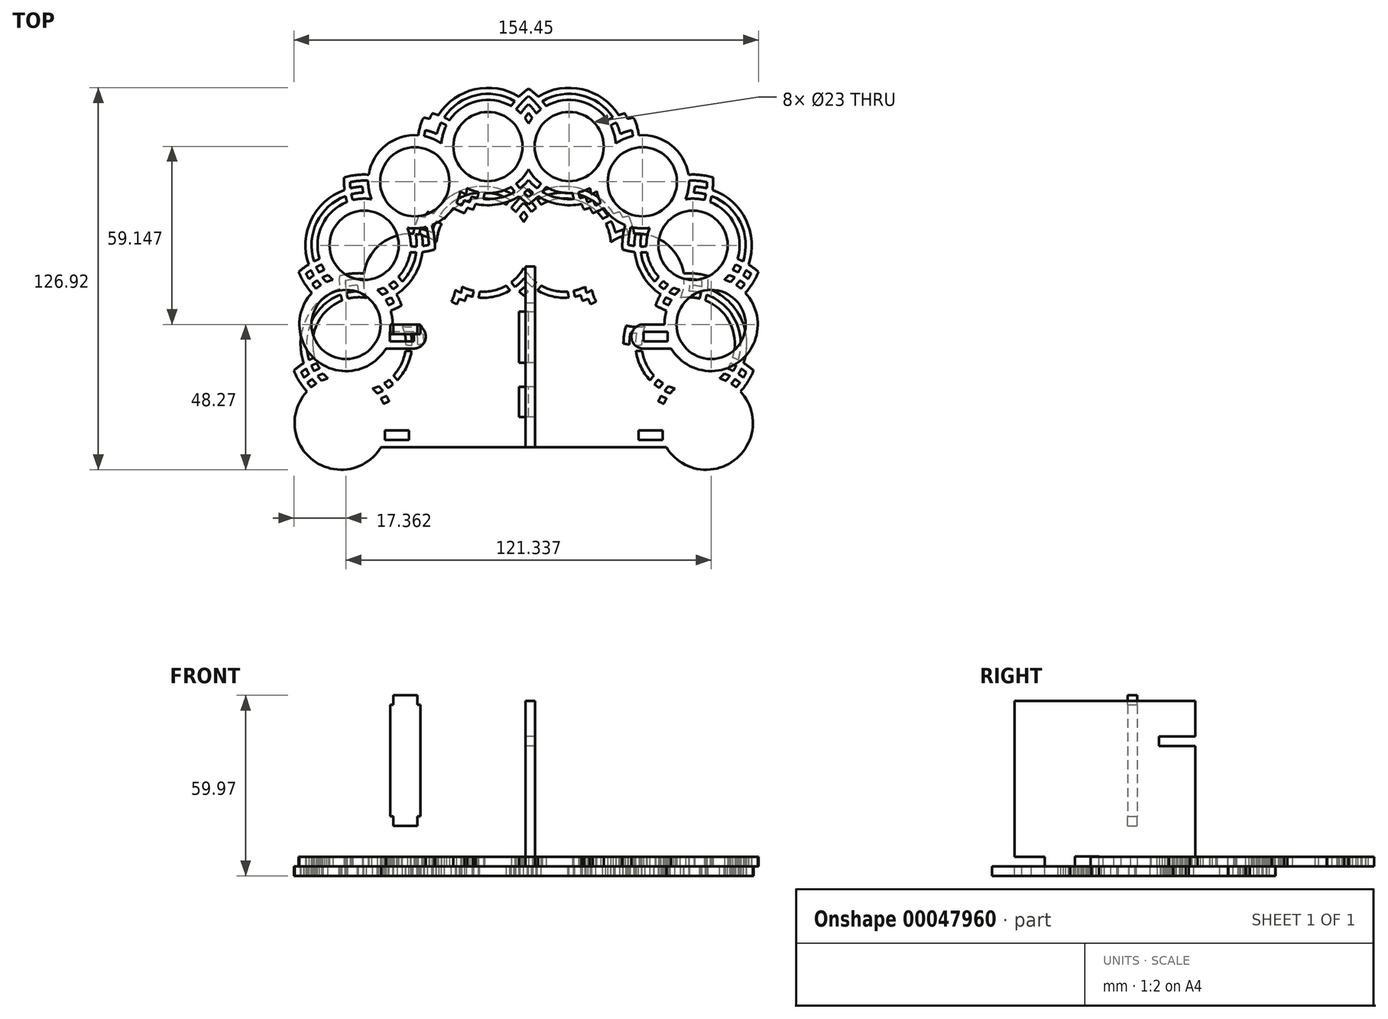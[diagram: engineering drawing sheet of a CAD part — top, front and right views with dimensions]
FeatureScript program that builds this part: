
annotation { "Feature Type Name" : "Feature", "Feature Type Description" : "" }
export const myFeature = defineFeature(function(context is Context, id is Id, definition is map)
    precondition{}
    {
        {
            var Q0;
            Q0=qCreatedBy(makeId("Top.planeOp"),FACE);
            var sketch = newSketch(context, id + "F0", { "sketchPlane" : qUnion([Q0])});
            skCircle(sketch, "E0", {"center": v(-59.67, 0) * mm, "radius": 11.5 * mm});
            skArc(sketch, "E1.0", {"start": v(-64.09, 14.86) * mm, "mid": v(-65.14, 14.5) * mm, "end": v(-66.16, 14.08) * mm});
            skArc(sketch, "E2.0", {"start": v(-66.82, 18.14) * mm, "mid": v(-67.75, 17.75) * mm, "end": v(-68.66, 17.3) * mm});
            skArc(sketch, "E3.0", {"start": v(-67.77, 19.91) * mm, "mid": v(-68.7, 19.52) * mm, "end": v(-69.59, 19.07) * mm});
            skArc(sketch, "E4.0", {"start": v(-65.62, 16.46) * mm, "mid": v(-66.58, 16.08) * mm, "end": v(-67.52, 15.64) * mm});
            skArc(sketch, "E5.0", {"start": v(-68.48, 21.78) * mm, "mid": v(-69.4, 21.39) * mm, "end": v(-70.32, 20.95) * mm});
            skArc(sketch, "E6.1.0", {"start": v(-52.15, 49.77) * mm, "mid": v(-56.25, 49.68) * mm, "end": v(-60.28, 48.87) * mm});
            skArc(sketch, "E6.1.1", {"start": v(-53.95, 43.82) * mm, "mid": v(-55.95, 43.67) * mm, "end": v(-57.92, 43.3) * mm});
            skArc(sketch, "E6.1.2", {"start": v(-52.32, 47.78) * mm, "mid": v(-55.34, 47.76) * mm, "end": v(-58.33, 47.31) * mm});
            skArc(sketch, "E6.1.3", {"start": v(-54.25, 45.81) * mm, "mid": v(-56.25, 45.65) * mm, "end": v(-58.22, 45.28) * mm});
            skArc(sketch, "E6.1.4", {"start": v(-51.2, 41.63) * mm, "mid": v(-54.34, 41.8) * mm, "end": v(-57.45, 41.35) * mm});
            skCircle(sketch, "E6.1.5", {"center": v(-53.66, 26.32) * mm, "radius": 11.5 * mm});
            skArc(sketch, "E6.2.0", {"start": v(-25.29, 67.9) * mm, "mid": v(-26.18, 68.38) * mm, "end": v(-27.08, 68.82) * mm});
            skArc(sketch, "E6.2.1", {"start": v(-29.5, 63.32) * mm, "mid": v(-31.36, 64.06) * mm, "end": v(-33.3, 64.57) * mm});
            skArc(sketch, "E6.2.2", {"start": v(-26.31, 66.19) * mm, "mid": v(-27.2, 66.65) * mm, "end": v(-28.1, 67.08) * mm});
            skArc(sketch, "E6.2.4", {"start": v(-27.97, 60.15) * mm, "mid": v(-30.72, 61.68) * mm, "end": v(-33.72, 62.62) * mm});
            skCircle(sketch, "E6.2.5", {"center": v(-36.83, 47.43) * mm, "radius": 11.5 * mm});
            skArc(sketch, "E6.3.0", {"start": v(6.78, 72.59) * mm, "mid": v(6.18, 73.4) * mm, "end": v(5.56, 74.19) * mm});
            skArc(sketch, "E6.3.1", {"start": v(2.22, 68.6) * mm, "mid": v(1.64, 69.46) * mm, "end": v(1, 70.28) * mm});
            skArc(sketch, "E6.3.2", {"start": v(5.11, 71.48) * mm, "mid": v(3.21, 73.83) * mm, "end": v(1, 75.88) * mm});
            skArc(sketch, "E6.3.3", {"start": v(3.6, 70.16) * mm, "mid": v(2.38, 71.76) * mm, "end": v(1, 73.22) * mm});
            skArc(sketch, "E6.3.4", {"start": v(1, 66.76) * mm, "mid": v(0.42, 67.7) * mm, "end": v(-0.22, 68.6) * mm});
            skCircle(sketch, "E6.3.5", {"center": v(-12.5, 59.15) * mm, "radius": 11.5 * mm});
            skArc(sketch, "E6.4.0", {"start": v(-4.78, 45.7) * mm, "mid": v(-4.18, 44.9) * mm, "end": v(-3.56, 44.1) * mm});
            skArc(sketch, "E6.4.1", {"start": v(1, 48.01) * mm, "mid": v(2.36, 46.54) * mm, "end": v(3.89, 45.23) * mm});
            skArc(sketch, "E6.4.2", {"start": v(-3.11, 46.81) * mm, "mid": v(-2.52, 46) * mm, "end": v(-1.89, 45.23) * mm});
            skArc(sketch, "E6.4.3", {"start": v(1, 45.08) * mm, "mid": v(1.74, 44.4) * mm, "end": v(2.52, 43.76) * mm});
            skArc(sketch, "E6.4.4", {"start": v(1, 51.53) * mm, "mid": v(2.82, 48.96) * mm, "end": v(5.11, 46.81) * mm});
            skCircle(sketch, "E6.4.5", {"center": v(14.5, 59.15) * mm, "radius": 11.5 * mm});
            skArc(sketch, "E6.5.0", {"start": v(15.63, 43.69) * mm, "mid": v(15.8, 42.7) * mm, "end": v(16.03, 41.71) * mm});
            skArc(sketch, "E6.5.1", {"start": v(21.46, 45.3) * mm, "mid": v(21.61, 44.27) * mm, "end": v(21.83, 43.26) * mm});
            skArc(sketch, "E6.5.2", {"start": v(17.6, 43.96) * mm, "mid": v(17.8, 42.98) * mm, "end": v(18.02, 42) * mm});
            skArc(sketch, "E6.5.3", {"start": v(19.96, 42.52) * mm, "mid": v(20.23, 41.56) * mm, "end": v(20.56, 40.61) * mm});
            skArc(sketch, "E6.5.4", {"start": v(23.66, 44.24) * mm, "mid": v(24.21, 42.27) * mm, "end": v(25.02, 40.4) * mm});
            skCircle(sketch, "E6.5.5", {"center": v(38.83, 47.43) * mm, "radius": 11.5 * mm});
            skArc(sketch, "E6.6.0", {"start": v(74.34, 12.07) * mm, "mid": v(76.06, 14.65) * mm, "end": v(77.42, 17.44) * mm});
            skArc(sketch, "E6.6.1", {"start": v(68.16, 14.08) * mm, "mid": v(68.86, 14.84) * mm, "end": v(69.52, 15.64) * mm});
            skArc(sketch, "E6.6.2", {"start": v(71.6, 11.9) * mm, "mid": v(72.26, 12.65) * mm, "end": v(72.87, 13.44) * mm});
            skArc(sketch, "E6.6.3", {"start": v(69.98, 13.08) * mm, "mid": v(70.64, 13.84) * mm, "end": v(71.27, 14.63) * mm});
            skArc(sketch, "E6.6.4", {"start": v(41.29, 32.13) * mm, "mid": v(40.41, 29.1) * mm, "end": v(40.16, 25.97) * mm});
            skCircle(sketch, "E6.6.5", {"center": v(55.66, 26.32) * mm, "radius": 11.5 * mm});
            skArc(sketch, "E6.7.0", {"start": v(44.28, 15.8) * mm, "mid": v(43.61, 15.04) * mm, "end": v(42.99, 14.26) * mm});
            skArc(sketch, "E6.7.2", {"start": v(45.73, 14.43) * mm, "mid": v(45.07, 13.67) * mm, "end": v(44.45, 12.88) * mm});
            skArc(sketch, "E6.7.3", {"start": v(47.35, 13.24) * mm, "mid": v(46.69, 12.48) * mm, "end": v(46.06, 11.7) * mm});
            skArc(sketch, "E6.7.4", {"start": v(51.24, 11.47) * mm, "mid": v(50.45, 10.7) * mm, "end": v(49.71, 9.86) * mm});
            skCircle(sketch, "E6.7.5", {"center": v(61.67, 0) * mm, "radius": 11.5 * mm});
            skPoint(sketch, "E6.center", {"position": v(1, 0) * mm});
            skLineSegment(sketch, "E6.anchor1", {"start": v(1, 0) * mm, "end": v(-59.67, 0) * mm, "construction": true});
            skLineSegment(sketch, "E6.anchor2", {"start": v(1, 0) * mm, "end": v(61.67, 0) * mm, "construction": true});
            skArc(sketch, "E7.trimOffspring", {"start": v(-21.66, 44.24) * mm, "mid": v(-20.76, 43.72) * mm, "end": v(-19.83, 43.26) * mm});
            skArc(sketch, "E8.trimOffspring", {"start": v(-20.42, 41.33) * mm, "mid": v(-19.5, 40.95) * mm, "end": v(-18.56, 40.61) * mm});
            skArc(sketch, "E9.trimOffspring", {"start": v(-23.02, 40.4) * mm, "mid": v(-22.13, 39.93) * mm, "end": v(-21.23, 39.5) * mm});
            skArc(sketch, "E10.trimOffspring", {"start": v(-24.04, 38.67) * mm, "mid": v(-22.23, 37.76) * mm, "end": v(-20.35, 37) * mm});
            skArc(sketch, "E11.trimOffspring", {"start": v(-38.34, 23.98) * mm, "mid": v(-37.33, 23.94) * mm, "end": v(-36.32, 23.94) * mm});
            skArc(sketch, "E12.trimOffspring", {"start": v(-38.16, 25.97) * mm, "mid": v(-37.16, 25.94) * mm, "end": v(-36.16, 25.94) * mm});
            skArc(sketch, "E13.trimOffspring", {"start": v(-36.54, 29.93) * mm, "mid": v(-35.53, 29.98) * mm, "end": v(-34.53, 30.08) * mm});
            skArc(sketch, "E14.trimOffspring", {"start": v(-44.85, 4.54) * mm, "mid": v(-43, 5.38) * mm, "end": v(-41.24, 6.37) * mm});
            skArc(sketch, "E15.trimOffspring", {"start": v(-45.56, 6.4) * mm, "mid": v(-44.64, 6.8) * mm, "end": v(-43.74, 7.25) * mm});
            skArc(sketch, "E16.trimOffspring", {"start": v(-46.5, 8.18) * mm, "mid": v(-45.58, 8.58) * mm, "end": v(-44.67, 9.02) * mm});
            skArc(sketch, "E17.trimOffspring", {"start": v(-47.71, 9.86) * mm, "mid": v(-46.75, 10.25) * mm, "end": v(-45.8, 10.68) * mm});
            skArc(sketch, "E18.trimOffspring", {"start": v(61.35, 40.74) * mm, "mid": v(61.62, 41.71) * mm, "end": v(61.84, 42.7) * mm});
            skArc(sketch, "E19.trimOffspring", {"start": v(59.45, 41.35) * mm, "mid": v(59.7, 42.32) * mm, "end": v(59.92, 43.3) * mm});
            skArc(sketch, "E20.trimOffspring", {"start": v(55.95, 43.82) * mm, "mid": v(56.13, 44.81) * mm, "end": v(56.25, 45.81) * mm});
            skArc(sketch, "E21.trimOffspring", {"start": v(38.54, 29.93) * mm, "mid": v(38.24, 27.95) * mm, "end": v(38.16, 25.94) * mm});
            skArc(sketch, "E22.trimOffspring", {"start": v(36.53, 30.08) * mm, "mid": v(36.24, 28.1) * mm, "end": v(36.16, 26.1) * mm});
            skArc(sketch, "E23.trimOffspring", {"start": v(33.13, 33.02) * mm, "mid": v(32.31, 29) * mm, "end": v(32.2, 24.88) * mm});
            skArc(sketch, "E24.trimOffspring", {"start": v(37.7, 62.9) * mm, "mid": v(37.02, 65.87) * mm, "end": v(35.95, 68.74) * mm});
            skArc(sketch, "E25.trimOffspring", {"start": v(35.72, 62.62) * mm, "mid": v(35.53, 63.6) * mm, "end": v(35.3, 64.57) * mm});
            skArc(sketch, "E26.trimOffspring", {"start": v(31.5, 63.32) * mm, "mid": v(30.9, 65.24) * mm, "end": v(30.1, 67.08) * mm});
            skArc(sketch, "E27.trimOffspring", {"start": v(29.97, 60.15) * mm, "mid": v(29.45, 63.25) * mm, "end": v(28.31, 66.19) * mm});
            skArc(sketch, "E28.trimOffspring", {"start": v(35.04, 32.4) * mm, "mid": v(34.39, 29.45) * mm, "end": v(34.16, 26.44) * mm});
            skArc(sketch, "E29.trimOffspring", {"start": v(53.2, 41.63) * mm, "mid": v(54.07, 44.65) * mm, "end": v(54.32, 47.78) * mm});
            skArc(sketch, "E30.trimOffspring", {"start": v(-19.46, 45.3) * mm, "mid": v(-17.58, 44.5) * mm, "end": v(-15.6, 43.96) * mm});
            skArc(sketch, "E31.trimOffspring", {"start": v(66.09, 14.86) * mm, "mid": v(66.88, 15.63) * mm, "end": v(67.62, 16.46) * mm});
            skArc(sketch, "E32.trimOffspring", {"start": v(-49.24, 11.47) * mm, "mid": v(-48.2, 11.82) * mm, "end": v(-47.17, 12.25) * mm});
            skArc(sketch, "E33.trimOffspring", {"start": v(-39.29, 32.13) * mm, "mid": v(-36.15, 31.95) * mm, "end": v(-33.04, 32.4) * mm});
            skArc(sketch, "E34.trimOffspring", {"start": v(-41.24, 6.37) * mm, "mid": v(-42, 8.25) * mm, "end": v(-42.95, 10.03) * mm});
            skArc(sketch, "E35.trimOffspring", {"start": v(-43.74, 7.25) * mm, "mid": v(-44.18, 8.15) * mm, "end": v(-44.67, 9.02) * mm});
            skArc(sketch, "E36.trimOffspring", {"start": v(77.42, 17.44) * mm, "mid": v(75.8, 18.77) * mm, "end": v(74.09, 19.95) * mm});
            skArc(sketch, "E37.trimOffspring", {"start": v(74.98, 16.89) * mm, "mid": v(74.17, 17.5) * mm, "end": v(73.33, 18.07) * mm});
            skArc(sketch, "E38.trimOffspring", {"start": v(74, 15.1) * mm, "mid": v(73.2, 15.72) * mm, "end": v(72.38, 16.3) * mm});
            skArc(sketch, "E39.trimOffspring", {"start": v(71.6, 11.9) * mm, "mid": v(70.8, 12.52) * mm, "end": v(69.98, 13.08) * mm});
            skArc(sketch, "E40.trimOffspring", {"start": v(-75.42, 17.44) * mm, "mid": v(-73.54, 13.79) * mm, "end": v(-71.05, 10.52) * mm});
            skArc(sketch, "E41.trimOffspring", {"start": v(-72.98, 16.89) * mm, "mid": v(-72.51, 15.98) * mm, "end": v(-72, 15.1) * mm});
            skArc(sketch, "E42.trimOffspring", {"start": v(-30.95, 70.19) * mm, "mid": v(-31.46, 69.29) * mm, "end": v(-31.92, 68.37) * mm});
            skArc(sketch, "E43.trimOffspring", {"start": v(-33.95, 68.74) * mm, "mid": v(-35.02, 65.87) * mm, "end": v(-35.7, 62.9) * mm});
            skArc(sketch, "E44.trimOffspring", {"start": v(1, 78.38) * mm, "mid": v(-0.65, 77.11) * mm, "end": v(-2.19, 75.7) * mm});
            skArc(sketch, "E45.trimOffspring", {"start": v(1, 75.88) * mm, "mid": v(-1.21, 73.83) * mm, "end": v(-3.11, 71.48) * mm});
            skArc(sketch, "E46.trimOffspring", {"start": v(62.28, 48.87) * mm, "mid": v(58.25, 49.68) * mm, "end": v(54.15, 49.77) * mm});
            skArc(sketch, "E47.trimOffspring", {"start": v(60.33, 47.31) * mm, "mid": v(57.34, 47.76) * mm, "end": v(54.32, 47.78) * mm});
            skArc(sketch, "E48.trimOffspring", {"start": v(22.35, 37) * mm, "mid": v(24.23, 37.76) * mm, "end": v(26.04, 38.67) * mm});
            skArc(sketch, "E49.trimOffspring", {"start": v(19.4, 38.21) * mm, "mid": v(20.39, 38.47) * mm, "end": v(21.36, 38.77) * mm});
            skArc(sketch, "E50.trimOffspring", {"start": v(1, 39.91) * mm, "mid": v(2.65, 41.18) * mm, "end": v(4.19, 42.6) * mm});
            skArc(sketch, "E51.trimOffspring", {"start": v(1, 42.41) * mm, "mid": v(1.78, 43.07) * mm, "end": v(2.52, 43.76) * mm});
            skArc(sketch, "E52.trimOffspring", {"start": v(43.24, 6.37) * mm, "mid": v(44.12, 5.85) * mm, "end": v(45.01, 5.37) * mm});
            skArc(sketch, "E53.trimOffspring", {"start": v(-30.2, 24.88) * mm, "mid": v(-30.31, 29) * mm, "end": v(-31.13, 33.02) * mm});
            skArc(sketch, "E54.trimOffspring", {"start": v(-32.16, 26.44) * mm, "mid": v(-32.39, 29.45) * mm, "end": v(-33.04, 32.4) * mm});
            skArc(sketch, "E55.trimOffspring", {"start": v(-54.25, 45.81) * mm, "mid": v(-54.13, 44.81) * mm, "end": v(-53.95, 43.82) * mm});
            skArc(sketch, "E56.trimOffspring", {"start": v(-58.33, 47.31) * mm, "mid": v(-58.3, 46.3) * mm, "end": v(-58.22, 45.28) * mm});
            skArc(sketch, "E57.trimOffspring", {"start": v(-60.28, 48.87) * mm, "mid": v(-60.32, 46.79) * mm, "end": v(-60.17, 44.7) * mm});
            skArc(sketch, "E58.trimOffspring", {"start": v(35.3, 64.57) * mm, "mid": v(33.36, 64.06) * mm, "end": v(31.5, 63.32) * mm});
            skArc(sketch, "E59.trimOffspring", {"start": v(35.95, 68.74) * mm, "mid": v(34.93, 68.58) * mm, "end": v(33.92, 68.37) * mm});
            skArc(sketch, "E60.trimOffspring", {"start": v(32.95, 70.19) * mm, "mid": v(31.96, 69.9) * mm, "end": v(30.97, 69.58) * mm});
            skArc(sketch, "E61.trimOffspring", {"start": v(-28.97, 69.58) * mm, "mid": v(-29.96, 69.9) * mm, "end": v(-30.95, 70.19) * mm});
            skArc(sketch, "E62.trimOffspring", {"start": v(-28.1, 67.08) * mm, "mid": v(-28.9, 65.24) * mm, "end": v(-29.5, 63.32) * mm});
            skArc(sketch, "E63.trimOffspring", {"start": v(-26.31, 66.19) * mm, "mid": v(-27.45, 63.25) * mm, "end": v(-27.97, 60.15) * mm});
            skArc(sketch, "E64.trimOffspring", {"start": v(-4.78, 72.59) * mm, "mid": v(-15.95, 74.26) * mm, "end": v(-25.29, 67.9) * mm});
            skArc(sketch, "E65.trimOffspring", {"start": v(-3.56, 74.19) * mm, "mid": v(-16.4, 76.2) * mm, "end": v(-27.08, 68.82) * mm});
            skArc(sketch, "E66.trimOffspring", {"start": v(-3.56, 74.19) * mm, "mid": v(-4.18, 73.4) * mm, "end": v(-4.78, 72.59) * mm});
            skArc(sketch, "E67.trimOffspring", {"start": v(4.19, 75.7) * mm, "mid": v(2.65, 77.11) * mm, "end": v(1, 78.38) * mm});
            skArc(sketch, "E68.trimOffspring", {"start": v(5.11, 71.48) * mm, "mid": v(4.33, 70.84) * mm, "end": v(3.6, 70.16) * mm});
            skArc(sketch, "E69.trimOffspring", {"start": v(29.08, 68.82) * mm, "mid": v(28.18, 68.38) * mm, "end": v(27.29, 67.9) * mm});
            skArc(sketch, "E70.trimOffspring", {"start": v(29.08, 68.82) * mm, "mid": v(18.4, 76.2) * mm, "end": v(5.56, 74.19) * mm});
            skArc(sketch, "E71.trimOffspring", {"start": v(27.29, 67.9) * mm, "mid": v(17.95, 74.26) * mm, "end": v(6.78, 72.59) * mm});
            skArc(sketch, "E72.trimOffspring", {"start": v(62.17, 44.7) * mm, "mid": v(62.32, 46.79) * mm, "end": v(62.28, 48.87) * mm});
            skArc(sketch, "E73.trimOffspring", {"start": v(59.92, 43.3) * mm, "mid": v(57.95, 43.67) * mm, "end": v(55.95, 43.82) * mm});
            skArc(sketch, "E74.trimOffspring", {"start": v(59.45, 41.35) * mm, "mid": v(56.34, 41.8) * mm, "end": v(53.2, 41.63) * mm});
            skArc(sketch, "E75.trimOffspring", {"start": v(72.32, 20.95) * mm, "mid": v(71.4, 21.39) * mm, "end": v(70.48, 21.78) * mm});
            skArc(sketch, "E76.trimOffspring", {"start": v(72.32, 20.95) * mm, "mid": v(71.43, 33.92) * mm, "end": v(61.84, 42.7) * mm});
            skArc(sketch, "E77.trimOffspring", {"start": v(70.48, 21.78) * mm, "mid": v(69.63, 33.05) * mm, "end": v(61.35, 40.74) * mm});
            skArc(sketch, "E78.trimOffspring", {"start": v(-59.84, 42.7) * mm, "mid": v(-59.62, 41.71) * mm, "end": v(-59.35, 40.74) * mm});
            skArc(sketch, "E79.trimOffspring", {"start": v(-59.84, 42.7) * mm, "mid": v(-69.43, 33.92) * mm, "end": v(-70.32, 20.95) * mm});
            skArc(sketch, "E80.trimOffspring", {"start": v(-59.35, 40.74) * mm, "mid": v(-67.63, 33.05) * mm, "end": v(-68.48, 21.78) * mm});
            skArc(sketch, "E81.trimOffspring", {"start": v(-72.09, 19.95) * mm, "mid": v(-73.8, 18.77) * mm, "end": v(-75.42, 17.44) * mm});
            skArc(sketch, "E82.trimOffspring", {"start": v(-69.59, 19.07) * mm, "mid": v(-69.15, 18.18) * mm, "end": v(-68.66, 17.3) * mm});
            skArc(sketch, "E83.trimOffspring", {"start": v(-67.77, 19.91) * mm, "mid": v(-67.33, 19.01) * mm, "end": v(-66.82, 18.14) * mm});
            skArc(sketch, "E84.trimOffspring", {"start": v(-36.16, 25.94) * mm, "mid": v(-36.24, 27.95) * mm, "end": v(-36.54, 29.93) * mm});
            skArc(sketch, "E85.trimOffspring", {"start": v(-34.3, 24.07) * mm, "mid": v(-32.23, 24.39) * mm, "end": v(-30.2, 24.88) * mm});
            skArc(sketch, "E86.trimOffspring", {"start": v(-38.16, 25.97) * mm, "mid": v(-38.41, 29.1) * mm, "end": v(-39.29, 32.13) * mm});
            skArc(sketch, "E87.trimOffspring", {"start": v(-42.28, 15.8) * mm, "mid": v(-39.7, 19.6) * mm, "end": v(-38.34, 23.98) * mm});
            skArc(sketch, "E88.trimOffspring", {"start": v(-40.99, 14.26) * mm, "mid": v(-37.9, 18.73) * mm, "end": v(-36.32, 23.94) * mm});
            skArc(sketch, "E89.trimOffspring", {"start": v(-40.99, 14.26) * mm, "mid": v(-41.61, 15.04) * mm, "end": v(-42.28, 15.8) * mm});
            skArc(sketch, "E90.trimOffspring", {"start": v(-21.23, 39.5) * mm, "mid": v(-20.8, 40.4) * mm, "end": v(-20.42, 41.33) * mm});
            skArc(sketch, "E91.trimOffspring", {"start": v(-20.35, 37) * mm, "mid": v(-19.83, 37.87) * mm, "end": v(-19.36, 38.77) * mm});
            skArc(sketch, "E92.trimOffspring", {"start": v(-17.4, 38.21) * mm, "mid": v(-16.99, 39.14) * mm, "end": v(-16.62, 40.09) * mm});
            skArc(sketch, "E93.trimOffspring", {"start": v(32.2, 24.88) * mm, "mid": v(34.23, 24.39) * mm, "end": v(36.3, 24.07) * mm});
            skArc(sketch, "E94.trimOffspring", {"start": v(34.16, 26.44) * mm, "mid": v(35.16, 26.25) * mm, "end": v(36.16, 26.1) * mm});
            skArc(sketch, "E95.trimOffspring", {"start": v(36.53, 30.08) * mm, "mid": v(37.53, 29.98) * mm, "end": v(38.54, 29.93) * mm});
            skArc(sketch, "E96.trimOffspring", {"start": v(18.02, 42) * mm, "mid": v(19, 42.23) * mm, "end": v(19.96, 42.52) * mm});
            skArc(sketch, "E97.trimOffspring", {"start": v(17.6, 43.96) * mm, "mid": v(19.58, 44.5) * mm, "end": v(21.46, 45.3) * mm});
            skArc(sketch, "E98.trimOffspring", {"start": v(5.56, 44.1) * mm, "mid": v(6.18, 44.9) * mm, "end": v(6.78, 45.7) * mm});
            skArc(sketch, "E99.trimOffspring", {"start": v(5.56, 44.1) * mm, "mid": v(10.6, 42.09) * mm, "end": v(16.03, 41.71) * mm});
            skArc(sketch, "E100.trimOffspring", {"start": v(6.78, 45.7) * mm, "mid": v(11.05, 44.04) * mm, "end": v(15.63, 43.69) * mm});
            skArc(sketch, "E101.trimOffspring", {"start": v(-14.03, 41.71) * mm, "mid": v(-13.8, 42.7) * mm, "end": v(-13.63, 43.69) * mm});
            skArc(sketch, "E102.trimOffspring", {"start": v(-14.03, 41.71) * mm, "mid": v(-8.6, 42.09) * mm, "end": v(-3.56, 44.1) * mm});
            skArc(sketch, "E103.trimOffspring", {"start": v(-13.63, 43.69) * mm, "mid": v(-9.05, 44.04) * mm, "end": v(-4.78, 45.7) * mm});
            skArc(sketch, "E104.trimOffspring", {"start": v(-3.11, 46.81) * mm, "mid": v(-0.82, 48.96) * mm, "end": v(1, 51.53) * mm});
            skArc(sketch, "E105.trimOffspring", {"start": v(-1.89, 45.23) * mm, "mid": v(-0.36, 46.54) * mm, "end": v(1, 48.01) * mm});
            skArc(sketch, "E106.trimOffspring", {"start": v(-2.19, 42.6) * mm, "mid": v(-0.65, 41.18) * mm, "end": v(1, 39.91) * mm});
            skArc(sketch, "E107.trimOffspring", {"start": v(38.32, 23.94) * mm, "mid": v(39.33, 23.94) * mm, "end": v(40.34, 23.98) * mm});
            skArc(sketch, "E108.trimOffspring", {"start": v(38.32, 23.94) * mm, "mid": v(39.9, 18.73) * mm, "end": v(42.99, 14.26) * mm});
            skArc(sketch, "E109.trimOffspring", {"start": v(40.34, 23.98) * mm, "mid": v(41.7, 19.6) * mm, "end": v(44.28, 15.8) * mm});
            skArc(sketch, "E110.trimOffspring", {"start": v(45.73, 14.43) * mm, "mid": v(46.52, 13.8) * mm, "end": v(47.35, 13.24) * mm});
            skArc(sketch, "E111.trimOffspring", {"start": v(44.45, 12.88) * mm, "mid": v(45.24, 12.26) * mm, "end": v(46.06, 11.7) * mm});
            skArc(sketch, "E112.trimOffspring", {"start": v(-2.19, 75.7) * mm, "mid": v(-16.84, 78.16) * mm, "end": v(-28.97, 69.58) * mm});
            skArc(sketch, "E113.trimOffspring", {"start": v(1, 73.22) * mm, "mid": v(-0.38, 71.76) * mm, "end": v(-1.6, 70.16) * mm});
            skArc(sketch, "E114.trimOffspring", {"start": v(-0.52, 43.76) * mm, "mid": v(0.26, 44.4) * mm, "end": v(1, 45.08) * mm});
            skArc(sketch, "E115.trimOffspring", {"start": v(4.19, 42.6) * mm, "mid": v(11.16, 39.94) * mm, "end": v(18.62, 40.09) * mm});
            skArc(sketch, "E116.trimOffspring", {"start": v(-0.52, 43.76) * mm, "mid": v(0.22, 43.07) * mm, "end": v(1, 42.41) * mm});
            skArc(sketch, "E117.trimOffspring", {"start": v(3.89, 45.23) * mm, "mid": v(4.52, 46) * mm, "end": v(5.11, 46.81) * mm});
            skArc(sketch, "E118.trimOffspring", {"start": v(-1.6, 70.16) * mm, "mid": v(-2.33, 70.84) * mm, "end": v(-3.11, 71.48) * mm});
            skArc(sketch, "E119.trimOffspring", {"start": v(1, 70.28) * mm, "mid": v(0.36, 69.46) * mm, "end": v(-0.22, 68.6) * mm});
            skArc(sketch, "E120.trimOffspring", {"start": v(2.22, 68.6) * mm, "mid": v(1.58, 67.7) * mm, "end": v(1, 66.76) * mm});
            skArc(sketch, "E121.trimOffspring", {"start": v(-35.7, 62.9) * mm, "mid": v(-46.5, 59.55) * mm, "end": v(-52.15, 49.77) * mm});
            skArc(sketch, "E122.trimOffspring", {"start": v(-33.3, 64.57) * mm, "mid": v(-33.53, 63.6) * mm, "end": v(-33.72, 62.62) * mm});
            skArc(sketch, "E123.trimOffspring", {"start": v(-31.92, 68.37) * mm, "mid": v(-32.93, 68.58) * mm, "end": v(-33.95, 68.74) * mm});
            skArc(sketch, "E124.trimOffspring", {"start": v(30.97, 69.58) * mm, "mid": v(18.84, 78.16) * mm, "end": v(4.19, 75.7) * mm});
            skArc(sketch, "E125.trimOffspring", {"start": v(30.1, 67.08) * mm, "mid": v(29.2, 66.65) * mm, "end": v(28.31, 66.19) * mm});
            skArc(sketch, "E126.trimOffspring", {"start": v(33.92, 68.37) * mm, "mid": v(33.46, 69.29) * mm, "end": v(32.95, 70.19) * mm});
            skArc(sketch, "E127.trimOffspring", {"start": v(35.72, 62.62) * mm, "mid": v(32.72, 61.68) * mm, "end": v(29.97, 60.15) * mm});
            skArc(sketch, "E128.trimOffspring", {"start": v(22.42, 41.33) * mm, "mid": v(22.8, 40.4) * mm, "end": v(23.23, 39.5) * mm});
            skArc(sketch, "E129.trimOffspring", {"start": v(21.83, 43.26) * mm, "mid": v(22.76, 43.72) * mm, "end": v(23.66, 44.24) * mm});
            skArc(sketch, "E130.trimOffspring", {"start": v(26.04, 38.67) * mm, "mid": v(29.16, 35.31) * mm, "end": v(33.13, 33.02) * mm});
            skArc(sketch, "E131.trimOffspring", {"start": v(23.23, 39.5) * mm, "mid": v(24.13, 39.93) * mm, "end": v(25.02, 40.4) * mm});
            skArc(sketch, "E132.trimOffspring", {"start": v(21.36, 38.77) * mm, "mid": v(21.83, 37.87) * mm, "end": v(22.35, 37) * mm});
            skArc(sketch, "E133.trimOffspring", {"start": v(20.56, 40.61) * mm, "mid": v(21.5, 40.95) * mm, "end": v(22.42, 41.33) * mm});
            skArc(sketch, "E134.trimOffspring", {"start": v(18.62, 40.09) * mm, "mid": v(18.99, 39.14) * mm, "end": v(19.4, 38.21) * mm});
            skArc(sketch, "E135.trimOffspring", {"start": v(-17.96, 42.52) * mm, "mid": v(-17, 42.23) * mm, "end": v(-16.02, 42) * mm});
            skArc(sketch, "E136.trimOffspring", {"start": v(-19.83, 43.26) * mm, "mid": v(-19.61, 44.27) * mm, "end": v(-19.46, 45.3) * mm});
            skArc(sketch, "E137.trimOffspring", {"start": v(-23.02, 40.4) * mm, "mid": v(-22.21, 42.27) * mm, "end": v(-21.66, 44.24) * mm});
            skArc(sketch, "E138.trimOffspring", {"start": v(-19.36, 38.77) * mm, "mid": v(-18.39, 38.47) * mm, "end": v(-17.4, 38.21) * mm});
            skArc(sketch, "E139.trimOffspring", {"start": v(-18.56, 40.61) * mm, "mid": v(-18.23, 41.56) * mm, "end": v(-17.96, 42.52) * mm});
            skArc(sketch, "E140.trimOffspring", {"start": v(-16.62, 40.09) * mm, "mid": v(-9.16, 39.94) * mm, "end": v(-2.19, 42.6) * mm});
            skArc(sketch, "E141.trimOffspring", {"start": v(-16.02, 42) * mm, "mid": v(-15.8, 42.98) * mm, "end": v(-15.6, 43.96) * mm});
            skArc(sketch, "E142.trimOffspring", {"start": v(38.16, 25.94) * mm, "mid": v(39.16, 25.94) * mm, "end": v(40.16, 25.97) * mm});
            skArc(sketch, "E143.trimOffspring", {"start": v(36.3, 24.07) * mm, "mid": v(39.06, 16.09) * mm, "end": v(44.95, 10.03) * mm});
            skArc(sketch, "E144.trimOffspring", {"start": v(35.04, 32.4) * mm, "mid": v(38.15, 31.95) * mm, "end": v(41.29, 32.13) * mm});
            skArc(sketch, "E145.trimOffspring", {"start": v(60.22, 45.28) * mm, "mid": v(60.3, 46.3) * mm, "end": v(60.33, 47.31) * mm});
            skArc(sketch, "E146.trimOffspring", {"start": v(60.22, 45.28) * mm, "mid": v(58.25, 45.65) * mm, "end": v(56.25, 45.81) * mm});
            skArc(sketch, "E147.trimOffspring", {"start": v(54.15, 49.77) * mm, "mid": v(48.5, 59.55) * mm, "end": v(37.7, 62.9) * mm});
            skArc(sketch, "E148.trimOffspring", {"start": v(-34.16, 26.1) * mm, "mid": v(-33.16, 26.25) * mm, "end": v(-32.16, 26.44) * mm});
            skArc(sketch, "E149.trimOffspring", {"start": v(-31.13, 33.02) * mm, "mid": v(-27.16, 35.31) * mm, "end": v(-24.04, 38.67) * mm});
            skArc(sketch, "E150.trimOffspring", {"start": v(-34.16, 26.1) * mm, "mid": v(-34.24, 28.1) * mm, "end": v(-34.53, 30.08) * mm});
            skArc(sketch, "E151.trimOffspring", {"start": v(-57.92, 43.3) * mm, "mid": v(-57.7, 42.32) * mm, "end": v(-57.45, 41.35) * mm});
            skArc(sketch, "E152.trimOffspring", {"start": v(-60.17, 44.7) * mm, "mid": v(-71.23, 34.78) * mm, "end": v(-72.09, 19.95) * mm});
            skArc(sketch, "E153.trimOffspring", {"start": v(-52.32, 47.78) * mm, "mid": v(-52.07, 44.65) * mm, "end": v(-51.2, 41.63) * mm});
            skArc(sketch, "E154.trimOffspring", {"start": v(-65.62, 16.46) * mm, "mid": v(-64.88, 15.63) * mm, "end": v(-64.09, 14.86) * mm});
            skArc(sketch, "E155.trimOffspring", {"start": v(-67.52, 15.64) * mm, "mid": v(-66.86, 14.84) * mm, "end": v(-66.16, 14.08) * mm});
            skArc(sketch, "E156.trimOffspring", {"start": v(-69.27, 14.63) * mm, "mid": v(-70.09, 14.06) * mm, "end": v(-70.87, 13.44) * mm});
            skArc(sketch, "E157.trimOffspring", {"start": v(-67.98, 13.08) * mm, "mid": v(-68.8, 12.52) * mm, "end": v(-69.6, 11.9) * mm});
            skArc(sketch, "E158.trimOffspring", {"start": v(-71.05, 10.52) * mm, "mid": v(-68.98, -12.4) * mm, "end": v(-46.4, -8) * mm});
            skArc(sketch, "E159.trimOffspring", {"start": v(-71.33, 18.07) * mm, "mid": v(-70.88, 17.17) * mm, "end": v(-70.38, 16.3) * mm});
            skArc(sketch, "E160.trimOffspring", {"start": v(-69.27, 14.63) * mm, "mid": v(-68.64, 13.84) * mm, "end": v(-67.98, 13.08) * mm});
            skArc(sketch, "E161.trimOffspring", {"start": v(-70.87, 13.44) * mm, "mid": v(-70.26, 12.65) * mm, "end": v(-69.6, 11.9) * mm});
            skArc(sketch, "E162.trimOffspring", {"start": v(-70.38, 16.3) * mm, "mid": v(-71.2, 15.72) * mm, "end": v(-72, 15.1) * mm});
            skArc(sketch, "E163.trimOffspring", {"start": v(-71.33, 18.07) * mm, "mid": v(-72.17, 17.5) * mm, "end": v(-72.98, 16.89) * mm});
            skArc(sketch, "E164.trimOffspring", {"start": v(71.59, 19.07) * mm, "mid": v(70.7, 19.52) * mm, "end": v(69.77, 19.91) * mm});
            skArc(sketch, "E165.trimOffspring", {"start": v(70.66, 17.3) * mm, "mid": v(69.75, 17.75) * mm, "end": v(68.82, 18.14) * mm});
            skArc(sketch, "E166.trimOffspring", {"start": v(69.52, 15.64) * mm, "mid": v(68.58, 16.08) * mm, "end": v(67.62, 16.46) * mm});
            skArc(sketch, "E167.trimOffspring", {"start": v(68.16, 14.08) * mm, "mid": v(67.14, 14.5) * mm, "end": v(66.09, 14.86) * mm});
            skArc(sketch, "E168.trimOffspring", {"start": v(70.66, 17.3) * mm, "mid": v(71.15, 18.18) * mm, "end": v(71.59, 19.07) * mm});
            skArc(sketch, "E169.trimOffspring", {"start": v(68.82, 18.14) * mm, "mid": v(69.33, 19.01) * mm, "end": v(69.77, 19.91) * mm});
            skArc(sketch, "E170.trimOffspring", {"start": v(72.38, 16.3) * mm, "mid": v(72.88, 17.17) * mm, "end": v(73.33, 18.07) * mm});
            skArc(sketch, "E171.trimOffspring", {"start": v(74, 15.1) * mm, "mid": v(74.51, 15.98) * mm, "end": v(74.98, 16.89) * mm});
            skArc(sketch, "E172.trimOffspring", {"start": v(74.09, 19.95) * mm, "mid": v(73.23, 34.78) * mm, "end": v(62.17, 44.7) * mm});
            skArc(sketch, "E173.trimOffspring", {"start": v(49.17, 12.25) * mm, "mid": v(50.2, 11.82) * mm, "end": v(51.24, 11.47) * mm});
            skArc(sketch, "E174.trimOffspring", {"start": v(47.8, 10.68) * mm, "mid": v(48.75, 10.25) * mm, "end": v(49.71, 9.86) * mm});
            skArc(sketch, "E175.trimOffspring", {"start": v(44.95, 10.03) * mm, "mid": v(44, 8.25) * mm, "end": v(43.24, 6.37) * mm});
            skArc(sketch, "E176.trimOffspring", {"start": v(46.67, 9.02) * mm, "mid": v(46.18, 8.15) * mm, "end": v(45.74, 7.25) * mm});
            skArc(sketch, "E177.trimOffspring", {"start": v(46.67, 9.02) * mm, "mid": v(47.58, 8.58) * mm, "end": v(48.5, 8.18) * mm});
            skArc(sketch, "E178.trimOffspring", {"start": v(45.74, 7.25) * mm, "mid": v(46.64, 6.8) * mm, "end": v(47.56, 6.4) * mm});
            skArc(sketch, "E179.trimOffspring", {"start": v(-45.35, 13.24) * mm, "mid": v(-44.52, 13.8) * mm, "end": v(-43.73, 14.43) * mm});
            skArc(sketch, "E180.trimOffspring", {"start": v(-44.06, 11.7) * mm, "mid": v(-43.24, 12.26) * mm, "end": v(-42.45, 12.88) * mm});
            skArc(sketch, "E181.trimOffspring", {"start": v(-45.8, 10.68) * mm, "mid": v(-46.47, 11.49) * mm, "end": v(-47.17, 12.25) * mm});
            skArc(sketch, "E182.trimOffspring", {"start": v(-47.71, 9.86) * mm, "mid": v(-48.45, 10.7) * mm, "end": v(-49.24, 11.47) * mm});
            skArc(sketch, "E183.trimOffspring", {"start": v(-42.45, 12.88) * mm, "mid": v(-43.07, 13.67) * mm, "end": v(-43.73, 14.43) * mm});
            skArc(sketch, "E184.trimOffspring", {"start": v(-44.06, 11.7) * mm, "mid": v(-44.69, 12.48) * mm, "end": v(-45.35, 13.24) * mm});
            skArc(sketch, "E185.trimOffspring", {"start": v(-42.95, 10.03) * mm, "mid": v(-37.06, 16.09) * mm, "end": v(-34.3, 24.07) * mm});
            skArc(sketch, "E186.trimOffspring", {"start": v(-45.56, 6.4) * mm, "mid": v(-46, 7.31) * mm, "end": v(-46.5, 8.18) * mm});
            skArc(sketch, "E187.0", {"start": v(72.87, 13.44) * mm, "mid": v(72.09, 14.06) * mm, "end": v(71.27, 14.63) * mm});
            skArc(sketch, "E188.0", {"start": v(43.24, 6.37) * mm, "mid": v(45, 5.38) * mm, "end": v(46.85, 4.54) * mm});
            skArc(sketch, "E189.trimOffspring", {"start": v(73.05, 10.52) * mm, "mid": v(73.71, 11.28) * mm, "end": v(74.34, 12.07) * mm});
            skArc(sketch, "E190.trimOffspring", {"start": v(49.17, 12.25) * mm, "mid": v(48.47, 11.49) * mm, "end": v(47.8, 10.68) * mm});
            skArc(sketch, "E191.trimOffspring", {"start": v(48.5, 8.18) * mm, "mid": v(48, 7.31) * mm, "end": v(47.56, 6.4) * mm});
            skArc(sketch, "E192.trimOffspring", {"start": v(46.85, 4.54) * mm, "mid": v(46.34, 2.3) * mm, "end": v(46.17, 0) * mm});
            skLineSegment(sketch, "E193", {"start": v(-44.17, 0) * mm, "end": v(-37.17, 0) * mm});
            skArc(sketch, "E194", {"start": v(-37.17, -8) * mm, "mid": v(-33.17, -4) * mm, "end": v(-37.17, 0) * mm});
            skLineSegment(sketch, "E195.rect.bottom", {"start": v(-37.17, -5.59) * mm, "end": v(-45.17, -5.59) * mm});
            skLineSegment(sketch, "E195.rect.top", {"start": v(-37.17, -2.41) * mm, "end": v(-45.17, -2.41) * mm});
            skLineSegment(sketch, "E195.rect.right", {"start": v(-45.17, -5.59) * mm, "end": v(-45.17, -2.41) * mm});
            skLineSegment(sketch, "E196", {"start": v(46.17, 0) * mm, "end": v(39.17, 0) * mm});
            skLineSegment(sketch, "E197", {"start": v(39.17, -2.41) * mm, "end": v(39.17, -4) * mm});
            skArc(sketch, "E198", {"start": v(39.17, 0) * mm, "mid": v(35.17, -4) * mm, "end": v(39.17, -8) * mm});
            skLineSegment(sketch, "E199.rect.bottom", {"start": v(47.17, -5.59) * mm, "end": v(39.17, -5.59) * mm});
            skLineSegment(sketch, "E199.rect.top", {"start": v(47.17, -2.41) * mm, "end": v(39.17, -2.41) * mm});
            skLineSegment(sketch, "E199.rect.left", {"start": v(47.17, -5.59) * mm, "end": v(47.17, -2.41) * mm});
            skLineSegment(sketch, "E199.rect.right", {"start": v(39.17, -5.59) * mm, "end": v(39.17, -4) * mm});
            skLineSegment(sketch, "E200", {"start": v(39.17, -8) * mm, "end": v(48.4, -8) * mm});
            skLineSegment(sketch, "E201", {"start": v(-37.17, -8) * mm, "end": v(-46.4, -8) * mm});
            skArc(sketch, "E202.trimOffspring", {"start": v(-44.17, 0) * mm, "mid": v(-44.34, 2.3) * mm, "end": v(-44.85, 4.54) * mm});
            skLineSegment(sketch, "E203", {"start": v(-37.17, -2.41) * mm, "end": v(-37.17, -5.59) * mm});
            skArc(sketch, "E204.trimOffspring", {"start": v(48.4, -8) * mm, "mid": v(70.98, -12.4) * mm, "end": v(73.05, 10.52) * mm});
            skLineSegment(sketch, "E205", {"start": v(-37.17, -8) * mm, "end": v(39.17, -8) * mm, "construction": true});
            skLineSegment(sketch, "E206", {"start": v(1, 39.91) * mm, "end": v(1, -8) * mm, "construction": true});
            skSolve(sketch);
        }
        {
            var Q0;
            Q0=makeQuery(id+"F0.imprint","IMPRINT",FACE,{"disambiguationData":[TD([[makeQuery(id+"F0.imprint","IMPRINT",EDGE,{"derivedFrom":sQuery(id+"F0.wireOp",EDGE,"E0")}),-1.0]])]});
            extrude(context, id + "F1", {"entities" : qUnion([Q0]), "depth" : 3.17 * mm});
        }
        {
            var Q0;
            Q0=qCreatedBy(makeId("Top.planeOp"),FACE);
            var sketch = newSketch(context, id + "F2", { "sketchPlane" : qUnion([Q0])});
            skArc(sketch, "E207.0", {"start": v(-65.7, -17.92) * mm, "mid": v(-66.75, -18.27) * mm, "end": v(-67.77, -18.7) * mm});
            skArc(sketch, "E208.0", {"start": v(-68.44, -14.63) * mm, "mid": v(-69.36, -15.03) * mm, "end": v(-70.27, -15.47) * mm});
            skArc(sketch, "E209.0", {"start": v(-69.39, -12.86) * mm, "mid": v(-70.3, -13.26) * mm, "end": v(-71.2, -13.7) * mm});
            skArc(sketch, "E210.0", {"start": v(-67.23, -16.31) * mm, "mid": v(-68.2, -16.7) * mm, "end": v(-69.13, -17.13) * mm});
            skArc(sketch, "E211.0", {"start": v(-70.1, -10.99) * mm, "mid": v(-71.02, -11.39) * mm, "end": v(-71.93, -11.82) * mm});
            skArc(sketch, "E212.1.0", {"start": v(-53.76, 17) * mm, "mid": v(-57.87, 16.9) * mm, "end": v(-61.9, 16.1) * mm});
            skArc(sketch, "E212.1.1", {"start": v(-55.56, 11.05) * mm, "mid": v(-57.57, 10.9) * mm, "end": v(-59.54, 10.52) * mm});
            skArc(sketch, "E212.1.2", {"start": v(-53.94, 15) * mm, "mid": v(-56.95, 14.98) * mm, "end": v(-59.94, 14.54) * mm});
            skArc(sketch, "E212.1.3", {"start": v(-55.86, 13.04) * mm, "mid": v(-57.86, 12.88) * mm, "end": v(-59.83, 12.51) * mm});
            skArc(sketch, "E212.1.4", {"start": v(-52.81, 8.85) * mm, "mid": v(-55.95, 9.04) * mm, "end": v(-59.06, 8.58) * mm});
            skArc(sketch, "E212.2.0", {"start": v(-26.9, 35.13) * mm, "mid": v(-27.8, 35.6) * mm, "end": v(-28.7, 36.05) * mm});
            skArc(sketch, "E212.2.1", {"start": v(-31.1, 30.55) * mm, "mid": v(-32.98, 31.29) * mm, "end": v(-34.92, 31.8) * mm});
            skArc(sketch, "E212.2.2", {"start": v(-27.92, 33.41) * mm, "mid": v(-28.8, 33.88) * mm, "end": v(-29.71, 34.3) * mm});
            skArc(sketch, "E212.2.4", {"start": v(-29.58, 27.38) * mm, "mid": v(-32.33, 28.9) * mm, "end": v(-35.33, 29.85) * mm});
            skArc(sketch, "E212.3.0", {"start": v(5.16, 39.81) * mm, "mid": v(4.57, 40.63) * mm, "end": v(3.94, 41.42) * mm});
            skArc(sketch, "E212.3.1", {"start": v(0.6, 35.84) * mm, "mid": v(0.02, 36.7) * mm, "end": v(-0.61, 37.51) * mm});
            skArc(sketch, "E212.3.2", {"start": v(3.5, 38.7) * mm, "mid": v(1.6, 41.05) * mm, "end": v(-0.61, 43.1) * mm});
            skArc(sketch, "E212.3.3", {"start": v(1.98, 37.39) * mm, "mid": v(0.76, 38.98) * mm, "end": v(-0.61, 40.45) * mm});
            skArc(sketch, "E212.3.4", {"start": v(-0.61, 34) * mm, "mid": v(-1.2, 34.93) * mm, "end": v(-1.84, 35.84) * mm});
            skArc(sketch, "E212.4.0", {"start": v(-6.4, 12.94) * mm, "mid": v(-5.8, 12.12) * mm, "end": v(-5.17, 11.33) * mm});
            skArc(sketch, "E212.4.1", {"start": v(-0.61, 15.24) * mm, "mid": v(0.75, 13.77) * mm, "end": v(2.28, 12.46) * mm});
            skArc(sketch, "E212.4.2", {"start": v(-4.72, 14.04) * mm, "mid": v(-4.13, 13.24) * mm, "end": v(-3.5, 12.46) * mm});
            skArc(sketch, "E212.4.3", {"start": v(-0.61, 12.3) * mm, "mid": v(0.13, 11.63) * mm, "end": v(0.9, 10.99) * mm});
            skArc(sketch, "E212.4.4", {"start": v(-0.61, 18.76) * mm, "mid": v(1.2, 16.2) * mm, "end": v(3.5, 14.04) * mm});
            skArc(sketch, "E212.5.0", {"start": v(14.01, 10.92) * mm, "mid": v(14.2, 9.92) * mm, "end": v(14.42, 8.94) * mm});
            skArc(sketch, "E212.5.1", {"start": v(19.84, 12.52) * mm, "mid": v(20, 11.5) * mm, "end": v(20.22, 10.48) * mm});
            skArc(sketch, "E212.5.2", {"start": v(16, 11.19) * mm, "mid": v(16.18, 10.2) * mm, "end": v(16.4, 9.23) * mm});
            skArc(sketch, "E212.5.3", {"start": v(18.34, 9.75) * mm, "mid": v(18.62, 8.79) * mm, "end": v(18.94, 7.84) * mm});
            skArc(sketch, "E212.5.4", {"start": v(22.05, 11.46) * mm, "mid": v(22.6, 9.5) * mm, "end": v(23.4, 7.62) * mm});
            skArc(sketch, "E212.6.0", {"start": v(72.73, -20.7) * mm, "mid": v(74.44, -18.12) * mm, "end": v(75.8, -15.33) * mm});
            skArc(sketch, "E212.6.1", {"start": v(66.55, -18.7) * mm, "mid": v(67.25, -17.94) * mm, "end": v(67.9, -17.13) * mm});
            skArc(sketch, "E212.6.2", {"start": v(69.99, -20.87) * mm, "mid": v(70.64, -20.12) * mm, "end": v(71.26, -19.33) * mm});
            skArc(sketch, "E212.6.3", {"start": v(68.36, -19.69) * mm, "mid": v(69.03, -18.93) * mm, "end": v(69.65, -18.14) * mm});
            skArc(sketch, "E212.6.4", {"start": v(39.68, -0.64) * mm, "mid": v(38.8, -3.66) * mm, "end": v(38.55, -6.8) * mm});
            skArc(sketch, "E212.7.0", {"start": v(42.66, -16.97) * mm, "mid": v(42, -17.73) * mm, "end": v(41.37, -18.52) * mm});
            skArc(sketch, "E212.7.2", {"start": v(44.11, -18.35) * mm, "mid": v(43.46, -19.1) * mm, "end": v(42.84, -19.9) * mm});
            skArc(sketch, "E212.7.3", {"start": v(45.74, -19.53) * mm, "mid": v(45.07, -20.3) * mm, "end": v(44.45, -21.08) * mm});
            skArc(sketch, "E212.7.4", {"start": v(49.63, -21.3) * mm, "mid": v(48.83, -22.08) * mm, "end": v(48.1, -22.9) * mm});
            skArc(sketch, "E213.trimOffspring", {"start": v(-23.27, 11.46) * mm, "mid": v(-22.37, 10.95) * mm, "end": v(-21.44, 10.48) * mm});
            skArc(sketch, "E214.trimOffspring", {"start": v(-22.04, 8.56) * mm, "mid": v(-21.11, 8.17) * mm, "end": v(-20.17, 7.84) * mm});
            skArc(sketch, "E215.trimOffspring", {"start": v(-24.63, 7.62) * mm, "mid": v(-23.75, 7.15) * mm, "end": v(-22.84, 6.73) * mm});
            skArc(sketch, "E216.trimOffspring", {"start": v(-39.95, -8.8) * mm, "mid": v(-38.94, -8.83) * mm, "end": v(-37.94, -8.83) * mm});
            skArc(sketch, "E217.trimOffspring", {"start": v(-39.78, -6.8) * mm, "mid": v(-38.78, -6.84) * mm, "end": v(-37.78, -6.83) * mm});
            skArc(sketch, "E218.trimOffspring", {"start": v(-38.15, -2.84) * mm, "mid": v(-37.14, -2.8) * mm, "end": v(-36.14, -2.69) * mm});
            skArc(sketch, "E219.trimOffspring", {"start": v(-47.17, -26.36) * mm, "mid": v(-46.25, -25.96) * mm, "end": v(-45.35, -25.52) * mm});
            skArc(sketch, "E220.trimOffspring", {"start": v(-48.12, -24.59) * mm, "mid": v(-47.2, -24.2) * mm, "end": v(-46.28, -23.75) * mm});
            skArc(sketch, "E221.trimOffspring", {"start": v(-49.33, -22.9) * mm, "mid": v(-48.36, -22.53) * mm, "end": v(-47.42, -22.09) * mm});
            skArc(sketch, "E222.trimOffspring", {"start": v(59.74, 7.97) * mm, "mid": v(60, 8.94) * mm, "end": v(60.23, 9.92) * mm});
            skArc(sketch, "E223.trimOffspring", {"start": v(57.84, 8.58) * mm, "mid": v(58.1, 9.55) * mm, "end": v(58.31, 10.52) * mm});
            skArc(sketch, "E224.trimOffspring", {"start": v(54.34, 11.05) * mm, "mid": v(54.52, 12.04) * mm, "end": v(54.64, 13.04) * mm});
            skArc(sketch, "E225.trimOffspring", {"start": v(36.92, -2.84) * mm, "mid": v(36.62, -4.82) * mm, "end": v(36.55, -6.83) * mm});
            skArc(sketch, "E226.trimOffspring", {"start": v(34.91, -2.69) * mm, "mid": v(34.63, -4.67) * mm, "end": v(34.55, -6.67) * mm});
            skArc(sketch, "E227.trimOffspring", {"start": v(36.09, 30.12) * mm, "mid": v(35.4, 33.1) * mm, "end": v(34.34, 35.97) * mm});
            skArc(sketch, "E228.trimOffspring", {"start": v(34.1, 29.85) * mm, "mid": v(33.92, 30.83) * mm, "end": v(33.7, 31.8) * mm});
            skArc(sketch, "E229.trimOffspring", {"start": v(29.88, 30.55) * mm, "mid": v(29.3, 32.47) * mm, "end": v(28.48, 34.3) * mm});
            skArc(sketch, "E230.trimOffspring", {"start": v(28.35, 27.38) * mm, "mid": v(27.83, 30.48) * mm, "end": v(26.7, 33.41) * mm});
            skArc(sketch, "E231.trimOffspring", {"start": v(33.42, -0.37) * mm, "mid": v(32.78, -3.32) * mm, "end": v(32.55, -6.33) * mm});
            skArc(sketch, "E232.trimOffspring", {"start": v(51.58, 8.85) * mm, "mid": v(52.46, 11.87) * mm, "end": v(52.7, 15) * mm});
            skArc(sketch, "E233.trimOffspring", {"start": v(-21.07, 12.52) * mm, "mid": v(-19.19, 11.73) * mm, "end": v(-17.22, 11.19) * mm});
            skArc(sketch, "E234.trimOffspring", {"start": v(64.48, -17.92) * mm, "mid": v(65.27, -17.14) * mm, "end": v(66, -16.31) * mm});
            skArc(sketch, "E235.trimOffspring", {"start": v(-50.85, -21.3) * mm, "mid": v(-49.8, -20.95) * mm, "end": v(-48.78, -20.52) * mm});
            skArc(sketch, "E236.trimOffspring", {"start": v(-40.9, -0.64) * mm, "mid": v(-37.76, -0.83) * mm, "end": v(-34.65, -0.37) * mm});
            skArc(sketch, "E237.trimOffspring", {"start": v(-45.35, -25.52) * mm, "mid": v(-45.8, -24.63) * mm, "end": v(-46.28, -23.75) * mm});
            skArc(sketch, "E238.trimOffspring", {"start": v(75.8, -15.33) * mm, "mid": v(74.2, -14) * mm, "end": v(72.48, -12.82) * mm});
            skArc(sketch, "E239.trimOffspring", {"start": v(73.36, -15.89) * mm, "mid": v(72.55, -15.28) * mm, "end": v(71.71, -14.7) * mm});
            skArc(sketch, "E240.trimOffspring", {"start": v(72.39, -17.67) * mm, "mid": v(71.6, -17.05) * mm, "end": v(70.77, -16.48) * mm});
            skArc(sketch, "E241.trimOffspring", {"start": v(69.99, -20.87) * mm, "mid": v(69.2, -20.25) * mm, "end": v(68.36, -19.69) * mm});
            skArc(sketch, "E242.trimOffspring", {"start": v(-77.03, -15.33) * mm, "mid": v(-75.15, -18.98) * mm, "end": v(-72.67, -22.25) * mm});
            skArc(sketch, "E243.trimOffspring", {"start": v(-74.6, -15.89) * mm, "mid": v(-74.12, -16.79) * mm, "end": v(-73.61, -17.67) * mm});
            skArc(sketch, "E244.trimOffspring", {"start": v(-32.56, 37.41) * mm, "mid": v(-33.07, 36.52) * mm, "end": v(-33.54, 35.6) * mm});
            skArc(sketch, "E245.trimOffspring", {"start": v(-35.57, 35.97) * mm, "mid": v(-36.63, 33.1) * mm, "end": v(-37.31, 30.12) * mm});
            skArc(sketch, "E246.trimOffspring", {"start": v(-0.61, 45.61) * mm, "mid": v(-2.27, 44.34) * mm, "end": v(-3.8, 42.92) * mm});
            skArc(sketch, "E247.trimOffspring", {"start": v(-0.61, 43.1) * mm, "mid": v(-2.82, 41.05) * mm, "end": v(-4.72, 38.7) * mm});
            skArc(sketch, "E248.trimOffspring", {"start": v(60.67, 16.1) * mm, "mid": v(56.64, 16.9) * mm, "end": v(52.53, 17) * mm});
            skArc(sketch, "E249.trimOffspring", {"start": v(58.71, 14.54) * mm, "mid": v(55.73, 14.98) * mm, "end": v(52.7, 15) * mm});
            skArc(sketch, "E250.trimOffspring", {"start": v(-0.61, 9.64) * mm, "mid": v(0.16, 10.3) * mm, "end": v(0.9, 10.99) * mm});
            skArc(sketch, "E251.trimOffspring", {"start": v(-33.77, -6.33) * mm, "mid": v(-34, -3.32) * mm, "end": v(-34.65, -0.37) * mm});
            skArc(sketch, "E252.trimOffspring", {"start": v(-55.86, 13.04) * mm, "mid": v(-55.74, 12.04) * mm, "end": v(-55.56, 11.05) * mm});
            skArc(sketch, "E253.trimOffspring", {"start": v(-59.94, 14.54) * mm, "mid": v(-59.9, 13.52) * mm, "end": v(-59.83, 12.51) * mm});
            skArc(sketch, "E254.trimOffspring", {"start": v(-61.9, 16.1) * mm, "mid": v(-61.93, 14.01) * mm, "end": v(-61.78, 11.93) * mm});
            skArc(sketch, "E255.trimOffspring", {"start": v(33.7, 31.8) * mm, "mid": v(31.75, 31.29) * mm, "end": v(29.88, 30.55) * mm});
            skArc(sketch, "E256.trimOffspring", {"start": v(34.34, 35.97) * mm, "mid": v(33.32, 35.8) * mm, "end": v(32.31, 35.6) * mm});
            skArc(sketch, "E257.trimOffspring", {"start": v(31.34, 37.41) * mm, "mid": v(30.34, 37.13) * mm, "end": v(29.36, 36.8) * mm});
            skArc(sketch, "E258.trimOffspring", {"start": v(-30.59, 36.8) * mm, "mid": v(-31.57, 37.13) * mm, "end": v(-32.56, 37.41) * mm});
            skArc(sketch, "E259.trimOffspring", {"start": v(-29.71, 34.3) * mm, "mid": v(-30.52, 32.47) * mm, "end": v(-31.1, 30.55) * mm});
            skArc(sketch, "E260.trimOffspring", {"start": v(-27.92, 33.41) * mm, "mid": v(-29.06, 30.48) * mm, "end": v(-29.58, 27.38) * mm});
            skArc(sketch, "E261.trimOffspring", {"start": v(-6.4, 39.81) * mm, "mid": v(-17.56, 41.49) * mm, "end": v(-26.9, 35.13) * mm});
            skArc(sketch, "E262.trimOffspring", {"start": v(-5.17, 41.42) * mm, "mid": v(-18, 43.44) * mm, "end": v(-28.7, 36.05) * mm});
            skArc(sketch, "E263.trimOffspring", {"start": v(-5.17, 41.42) * mm, "mid": v(-5.8, 40.63) * mm, "end": v(-6.4, 39.81) * mm});
            skArc(sketch, "E264.trimOffspring", {"start": v(2.57, 42.92) * mm, "mid": v(1.04, 44.34) * mm, "end": v(-0.61, 45.61) * mm});
            skArc(sketch, "E265.trimOffspring", {"start": v(3.5, 38.7) * mm, "mid": v(2.72, 38.07) * mm, "end": v(1.98, 37.39) * mm});
            skArc(sketch, "E266.trimOffspring", {"start": v(27.47, 36.05) * mm, "mid": v(26.56, 35.6) * mm, "end": v(25.68, 35.13) * mm});
            skArc(sketch, "E267.trimOffspring", {"start": v(27.47, 36.05) * mm, "mid": v(16.78, 43.44) * mm, "end": v(3.94, 41.42) * mm});
            skArc(sketch, "E268.trimOffspring", {"start": v(25.68, 35.13) * mm, "mid": v(16.34, 41.49) * mm, "end": v(5.16, 39.81) * mm});
            skArc(sketch, "E269.trimOffspring", {"start": v(60.55, 11.93) * mm, "mid": v(60.7, 14.01) * mm, "end": v(60.67, 16.1) * mm});
            skArc(sketch, "E270.trimOffspring", {"start": v(58.31, 10.52) * mm, "mid": v(56.34, 10.9) * mm, "end": v(54.34, 11.05) * mm});
            skArc(sketch, "E271.trimOffspring", {"start": v(57.84, 8.58) * mm, "mid": v(54.72, 9.04) * mm, "end": v(51.58, 8.85) * mm});
            skArc(sketch, "E272.trimOffspring", {"start": v(70.7, -11.82) * mm, "mid": v(69.8, -11.39) * mm, "end": v(68.87, -10.99) * mm});
            skArc(sketch, "E273.trimOffspring", {"start": v(70.7, -11.82) * mm, "mid": v(69.81, 1.14) * mm, "end": v(60.23, 9.92) * mm});
            skArc(sketch, "E274.trimOffspring", {"start": v(68.87, -10.99) * mm, "mid": v(68.01, 0.28) * mm, "end": v(59.74, 7.97) * mm});
            skArc(sketch, "E275.trimOffspring", {"start": v(-61.46, 9.92) * mm, "mid": v(-61.23, 8.94) * mm, "end": v(-60.97, 7.97) * mm});
            skArc(sketch, "E276.trimOffspring", {"start": v(-61.46, 9.92) * mm, "mid": v(-71.04, 1.14) * mm, "end": v(-71.93, -11.82) * mm});
            skArc(sketch, "E277.trimOffspring", {"start": v(-60.97, 7.97) * mm, "mid": v(-69.24, 0.28) * mm, "end": v(-70.1, -10.99) * mm});
            skArc(sketch, "E278.trimOffspring", {"start": v(-73.7, -12.82) * mm, "mid": v(-75.42, -14) * mm, "end": v(-77.03, -15.33) * mm});
            skArc(sketch, "E279.trimOffspring", {"start": v(-71.2, -13.7) * mm, "mid": v(-70.76, -14.6) * mm, "end": v(-70.27, -15.47) * mm});
            skArc(sketch, "E280.trimOffspring", {"start": v(-69.39, -12.86) * mm, "mid": v(-68.94, -13.76) * mm, "end": v(-68.44, -14.63) * mm});
            skArc(sketch, "E281.trimOffspring", {"start": v(-37.78, -6.83) * mm, "mid": v(-37.85, -4.82) * mm, "end": v(-38.15, -2.84) * mm});
            skArc(sketch, "E282.trimOffspring", {"start": v(-39.78, -6.8) * mm, "mid": v(-40.03, -3.66) * mm, "end": v(-40.9, -0.64) * mm});
            skArc(sketch, "E283.trimOffspring", {"start": v(-43.89, -16.97) * mm, "mid": v(-41.3, -13.17) * mm, "end": v(-39.95, -8.8) * mm});
            skArc(sketch, "E284.trimOffspring", {"start": v(-42.6, -18.52) * mm, "mid": v(-39.5, -14.04) * mm, "end": v(-37.94, -8.83) * mm});
            skArc(sketch, "E285.trimOffspring", {"start": v(-42.6, -18.52) * mm, "mid": v(-43.23, -17.73) * mm, "end": v(-43.89, -16.97) * mm});
            skArc(sketch, "E286.trimOffspring", {"start": v(-22.84, 6.73) * mm, "mid": v(-22.41, 7.63) * mm, "end": v(-22.04, 8.56) * mm});
            skArc(sketch, "E287.trimOffspring", {"start": v(32.55, -6.33) * mm, "mid": v(33.54, -6.52) * mm, "end": v(34.55, -6.67) * mm});
            skArc(sketch, "E288.trimOffspring", {"start": v(34.91, -2.69) * mm, "mid": v(35.92, -2.8) * mm, "end": v(36.92, -2.84) * mm});
            skArc(sketch, "E289.trimOffspring", {"start": v(16.4, 9.23) * mm, "mid": v(17.38, 9.46) * mm, "end": v(18.34, 9.75) * mm});
            skArc(sketch, "E290.trimOffspring", {"start": v(16, 11.19) * mm, "mid": v(17.96, 11.73) * mm, "end": v(19.84, 12.52) * mm});
            skArc(sketch, "E291.trimOffspring", {"start": v(3.94, 11.33) * mm, "mid": v(4.57, 12.12) * mm, "end": v(5.16, 12.94) * mm});
            skArc(sketch, "E292.trimOffspring", {"start": v(3.94, 11.33) * mm, "mid": v(9, 9.31) * mm, "end": v(14.42, 8.94) * mm});
            skArc(sketch, "E293.trimOffspring", {"start": v(5.16, 12.94) * mm, "mid": v(9.44, 11.26) * mm, "end": v(14.01, 10.92) * mm});
            skArc(sketch, "E294.trimOffspring", {"start": v(-15.65, 8.94) * mm, "mid": v(-15.42, 9.92) * mm, "end": v(-15.24, 10.92) * mm});
            skArc(sketch, "E295.trimOffspring", {"start": v(-15.65, 8.94) * mm, "mid": v(-10.22, 9.31) * mm, "end": v(-5.17, 11.33) * mm});
            skArc(sketch, "E296.trimOffspring", {"start": v(-15.24, 10.92) * mm, "mid": v(-10.66, 11.26) * mm, "end": v(-6.4, 12.94) * mm});
            skArc(sketch, "E297.trimOffspring", {"start": v(-4.72, 14.04) * mm, "mid": v(-2.43, 16.2) * mm, "end": v(-0.61, 18.76) * mm});
            skArc(sketch, "E298.trimOffspring", {"start": v(-3.5, 12.46) * mm, "mid": v(-1.98, 13.77) * mm, "end": v(-0.61, 15.24) * mm});
            skArc(sketch, "E299.trimOffspring", {"start": v(36.71, -8.83) * mm, "mid": v(37.72, -8.83) * mm, "end": v(38.72, -8.8) * mm});
            skArc(sketch, "E300.trimOffspring", {"start": v(36.71, -8.83) * mm, "mid": v(38.28, -14.04) * mm, "end": v(41.37, -18.52) * mm});
            skArc(sketch, "E301.trimOffspring", {"start": v(38.72, -8.8) * mm, "mid": v(40.08, -13.17) * mm, "end": v(42.66, -16.97) * mm});
            skArc(sketch, "E302.trimOffspring", {"start": v(44.11, -18.35) * mm, "mid": v(44.9, -18.97) * mm, "end": v(45.74, -19.53) * mm});
            skArc(sketch, "E303.trimOffspring", {"start": v(42.84, -19.9) * mm, "mid": v(43.63, -20.5) * mm, "end": v(44.45, -21.08) * mm});
            skArc(sketch, "E304.trimOffspring", {"start": v(-3.8, 42.92) * mm, "mid": v(-18.45, 45.39) * mm, "end": v(-30.59, 36.8) * mm});
            skArc(sketch, "E305.trimOffspring", {"start": v(-0.61, 40.45) * mm, "mid": v(-1.99, 38.98) * mm, "end": v(-3.2, 37.39) * mm});
            skArc(sketch, "E306.trimOffspring", {"start": v(-2.13, 10.99) * mm, "mid": v(-1.36, 11.63) * mm, "end": v(-0.61, 12.3) * mm});
            skArc(sketch, "E307.trimOffspring", {"start": v(-2.13, 10.99) * mm, "mid": v(-1.39, 10.3) * mm, "end": v(-0.61, 9.64) * mm});
            skArc(sketch, "E308.trimOffspring", {"start": v(2.28, 12.46) * mm, "mid": v(2.9, 13.24) * mm, "end": v(3.5, 14.04) * mm});
            skArc(sketch, "E309.trimOffspring", {"start": v(-3.2, 37.39) * mm, "mid": v(-3.94, 38.07) * mm, "end": v(-4.72, 38.7) * mm});
            skArc(sketch, "E310.trimOffspring", {"start": v(-0.61, 37.51) * mm, "mid": v(-1.25, 36.7) * mm, "end": v(-1.84, 35.84) * mm});
            skArc(sketch, "E311.trimOffspring", {"start": v(0.6, 35.84) * mm, "mid": v(-0.04, 34.93) * mm, "end": v(-0.61, 34) * mm});
            skArc(sketch, "E312.trimOffspring", {"start": v(-37.31, 30.12) * mm, "mid": v(-48.1, 26.78) * mm, "end": v(-53.76, 17) * mm});
            skArc(sketch, "E313.trimOffspring", {"start": v(-34.92, 31.8) * mm, "mid": v(-35.15, 30.83) * mm, "end": v(-35.33, 29.85) * mm});
            skArc(sketch, "E314.trimOffspring", {"start": v(-33.54, 35.6) * mm, "mid": v(-34.55, 35.8) * mm, "end": v(-35.57, 35.97) * mm});
            skArc(sketch, "E315.trimOffspring", {"start": v(29.36, 36.8) * mm, "mid": v(17.23, 45.39) * mm, "end": v(2.57, 42.92) * mm});
            skArc(sketch, "E316.trimOffspring", {"start": v(28.48, 34.3) * mm, "mid": v(27.58, 33.88) * mm, "end": v(26.7, 33.41) * mm});
            skArc(sketch, "E317.trimOffspring", {"start": v(32.31, 35.6) * mm, "mid": v(31.85, 36.52) * mm, "end": v(31.34, 37.41) * mm});
            skArc(sketch, "E318.trimOffspring", {"start": v(34.1, 29.85) * mm, "mid": v(31.1, 28.9) * mm, "end": v(28.35, 27.38) * mm});
            skArc(sketch, "E319.trimOffspring", {"start": v(20.81, 8.56) * mm, "mid": v(21.19, 7.63) * mm, "end": v(21.61, 6.73) * mm});
            skArc(sketch, "E320.trimOffspring", {"start": v(20.22, 10.48) * mm, "mid": v(21.15, 10.95) * mm, "end": v(22.05, 11.46) * mm});
            skArc(sketch, "E321.trimOffspring", {"start": v(21.61, 6.73) * mm, "mid": v(22.52, 7.15) * mm, "end": v(23.4, 7.62) * mm});
            skArc(sketch, "E322.trimOffspring", {"start": v(18.94, 7.84) * mm, "mid": v(19.89, 8.17) * mm, "end": v(20.81, 8.56) * mm});
            skArc(sketch, "E323.trimOffspring", {"start": v(-19.57, 9.75) * mm, "mid": v(-18.6, 9.46) * mm, "end": v(-17.64, 9.23) * mm});
            skArc(sketch, "E324.trimOffspring", {"start": v(-21.44, 10.48) * mm, "mid": v(-21.23, 11.5) * mm, "end": v(-21.07, 12.52) * mm});
            skArc(sketch, "E325.trimOffspring", {"start": v(-24.63, 7.62) * mm, "mid": v(-23.82, 9.5) * mm, "end": v(-23.27, 11.46) * mm});
            skArc(sketch, "E326.trimOffspring", {"start": v(-20.17, 7.84) * mm, "mid": v(-19.85, 8.79) * mm, "end": v(-19.57, 9.75) * mm});
            skArc(sketch, "E327.trimOffspring", {"start": v(-17.64, 9.23) * mm, "mid": v(-17.4, 10.2) * mm, "end": v(-17.22, 11.19) * mm});
            skArc(sketch, "E328.trimOffspring", {"start": v(36.55, -6.83) * mm, "mid": v(37.55, -6.84) * mm, "end": v(38.55, -6.8) * mm});
            skArc(sketch, "E329.trimOffspring", {"start": v(33.42, -0.37) * mm, "mid": v(36.54, -0.83) * mm, "end": v(39.68, -0.64) * mm});
            skArc(sketch, "E330.trimOffspring", {"start": v(58.6, 12.51) * mm, "mid": v(58.68, 13.52) * mm, "end": v(58.71, 14.54) * mm});
            skArc(sketch, "E331.trimOffspring", {"start": v(58.6, 12.51) * mm, "mid": v(56.64, 12.88) * mm, "end": v(54.64, 13.04) * mm});
            skArc(sketch, "E332.trimOffspring", {"start": v(52.53, 17) * mm, "mid": v(46.88, 26.78) * mm, "end": v(36.09, 30.12) * mm});
            skArc(sketch, "E333.trimOffspring", {"start": v(-35.78, -6.67) * mm, "mid": v(-34.77, -6.52) * mm, "end": v(-33.77, -6.33) * mm});
            skArc(sketch, "E334.trimOffspring", {"start": v(-35.78, -6.67) * mm, "mid": v(-35.85, -4.67) * mm, "end": v(-36.14, -2.69) * mm});
            skArc(sketch, "E335.trimOffspring", {"start": v(-59.54, 10.52) * mm, "mid": v(-59.32, 9.55) * mm, "end": v(-59.06, 8.58) * mm});
            skArc(sketch, "E336.trimOffspring", {"start": v(-61.78, 11.93) * mm, "mid": v(-72.84, 2.01) * mm, "end": v(-73.7, -12.82) * mm});
            skArc(sketch, "E337.trimOffspring", {"start": v(-53.94, 15) * mm, "mid": v(-53.69, 11.87) * mm, "end": v(-52.81, 8.85) * mm});
            skArc(sketch, "E338.trimOffspring", {"start": v(-67.23, -16.31) * mm, "mid": v(-66.5, -17.14) * mm, "end": v(-65.7, -17.92) * mm});
            skArc(sketch, "E339.trimOffspring", {"start": v(-69.13, -17.13) * mm, "mid": v(-68.48, -17.94) * mm, "end": v(-67.77, -18.7) * mm});
            skArc(sketch, "E340.trimOffspring", {"start": v(-70.88, -18.14) * mm, "mid": v(-71.7, -18.71) * mm, "end": v(-72.49, -19.33) * mm});
            skArc(sketch, "E341.trimOffspring", {"start": v(-69.6, -19.69) * mm, "mid": v(-70.42, -20.25) * mm, "end": v(-71.22, -20.87) * mm});
            skArc(sketch, "E342.trimOffspring", {"start": v(-72.67, -22.25) * mm, "mid": v(-70.59, -45.17) * mm, "end": v(-48, -40.77) * mm});
            skArc(sketch, "E343.trimOffspring", {"start": v(-72.94, -14.7) * mm, "mid": v(-72.5, -15.6) * mm, "end": v(-72, -16.48) * mm});
            skArc(sketch, "E344.trimOffspring", {"start": v(-70.88, -18.14) * mm, "mid": v(-70.26, -18.93) * mm, "end": v(-69.6, -19.69) * mm});
            skArc(sketch, "E345.trimOffspring", {"start": v(-72.49, -19.33) * mm, "mid": v(-71.87, -20.12) * mm, "end": v(-71.22, -20.87) * mm});
            skArc(sketch, "E346.trimOffspring", {"start": v(-72, -16.48) * mm, "mid": v(-72.82, -17.05) * mm, "end": v(-73.61, -17.67) * mm});
            skArc(sketch, "E347.trimOffspring", {"start": v(-72.94, -14.7) * mm, "mid": v(-73.78, -15.28) * mm, "end": v(-74.6, -15.89) * mm});
            skArc(sketch, "E348.trimOffspring", {"start": v(69.98, -13.7) * mm, "mid": v(69.08, -13.26) * mm, "end": v(68.16, -12.86) * mm});
            skArc(sketch, "E349.trimOffspring", {"start": v(69.04, -15.47) * mm, "mid": v(68.14, -15.03) * mm, "end": v(67.21, -14.63) * mm});
            skArc(sketch, "E350.trimOffspring", {"start": v(67.9, -17.13) * mm, "mid": v(66.97, -16.7) * mm, "end": v(66, -16.31) * mm});
            skArc(sketch, "E351.trimOffspring", {"start": v(66.55, -18.7) * mm, "mid": v(65.53, -18.27) * mm, "end": v(64.48, -17.92) * mm});
            skArc(sketch, "E352.trimOffspring", {"start": v(69.04, -15.47) * mm, "mid": v(69.54, -14.6) * mm, "end": v(69.98, -13.7) * mm});
            skArc(sketch, "E353.trimOffspring", {"start": v(67.21, -14.63) * mm, "mid": v(67.71, -13.76) * mm, "end": v(68.16, -12.86) * mm});
            skArc(sketch, "E354.trimOffspring", {"start": v(70.77, -16.48) * mm, "mid": v(71.26, -15.6) * mm, "end": v(71.71, -14.7) * mm});
            skArc(sketch, "E355.trimOffspring", {"start": v(72.39, -17.67) * mm, "mid": v(72.9, -16.79) * mm, "end": v(73.36, -15.89) * mm});
            skArc(sketch, "E356.trimOffspring", {"start": v(72.48, -12.82) * mm, "mid": v(71.62, 2.01) * mm, "end": v(60.55, 11.93) * mm});
            skArc(sketch, "E357.trimOffspring", {"start": v(47.56, -20.52) * mm, "mid": v(48.58, -20.95) * mm, "end": v(49.63, -21.3) * mm});
            skArc(sketch, "E358.trimOffspring", {"start": v(46.2, -22.09) * mm, "mid": v(47.13, -22.53) * mm, "end": v(48.1, -22.9) * mm});
            skArc(sketch, "E359.trimOffspring", {"start": v(45.06, -23.75) * mm, "mid": v(44.57, -24.63) * mm, "end": v(44.13, -25.52) * mm});
            skArc(sketch, "E360.trimOffspring", {"start": v(45.06, -23.75) * mm, "mid": v(45.96, -24.2) * mm, "end": v(46.9, -24.59) * mm});
            skArc(sketch, "E361.trimOffspring", {"start": v(44.13, -25.52) * mm, "mid": v(45.02, -25.96) * mm, "end": v(45.94, -26.36) * mm});
            skArc(sketch, "E362.trimOffspring", {"start": v(-46.96, -19.53) * mm, "mid": v(-46.13, -18.97) * mm, "end": v(-45.34, -18.35) * mm});
            skArc(sketch, "E363.trimOffspring", {"start": v(-45.67, -21.08) * mm, "mid": v(-44.85, -20.5) * mm, "end": v(-44.07, -19.9) * mm});
            skArc(sketch, "E364.trimOffspring", {"start": v(-47.42, -22.09) * mm, "mid": v(-48.08, -21.29) * mm, "end": v(-48.78, -20.52) * mm});
            skArc(sketch, "E365.trimOffspring", {"start": v(-49.33, -22.9) * mm, "mid": v(-50.06, -22.08) * mm, "end": v(-50.85, -21.3) * mm});
            skArc(sketch, "E366.trimOffspring", {"start": v(-44.07, -19.9) * mm, "mid": v(-44.69, -19.1) * mm, "end": v(-45.34, -18.35) * mm});
            skArc(sketch, "E367.trimOffspring", {"start": v(-45.67, -21.08) * mm, "mid": v(-46.3, -20.3) * mm, "end": v(-46.96, -19.53) * mm});
            skArc(sketch, "E368.trimOffspring", {"start": v(-47.17, -26.36) * mm, "mid": v(-47.61, -25.46) * mm, "end": v(-48.12, -24.59) * mm});
            skArc(sketch, "E369.0", {"start": v(71.26, -19.33) * mm, "mid": v(70.47, -18.71) * mm, "end": v(69.65, -18.14) * mm});
            skArc(sketch, "E370.trimOffspring", {"start": v(71.44, -22.25) * mm, "mid": v(72.1, -21.5) * mm, "end": v(72.73, -20.7) * mm});
            skArc(sketch, "E371.trimOffspring", {"start": v(47.56, -20.52) * mm, "mid": v(46.85, -21.29) * mm, "end": v(46.2, -22.09) * mm});
            skArc(sketch, "E372.trimOffspring", {"start": v(46.9, -24.59) * mm, "mid": v(46.39, -25.46) * mm, "end": v(45.94, -26.36) * mm});
            skLineSegment(sketch, "E373.rect.bottom", {"start": v(-38.78, -38.42) * mm, "end": v(-46.78, -38.42) * mm});
            skLineSegment(sketch, "E373.rect.top", {"start": v(-38.78, -35.24) * mm, "end": v(-46.78, -35.24) * mm});
            skLineSegment(sketch, "E373.rect.right", {"start": v(-46.78, -38.42) * mm, "end": v(-46.78, -35.24) * mm});
            skLineSegment(sketch, "E374.rect.bottom", {"start": v(45.56, -38.42) * mm, "end": v(37.56, -38.42) * mm});
            skLineSegment(sketch, "E374.rect.top", {"start": v(45.56, -35.24) * mm, "end": v(37.56, -35.24) * mm});
            skLineSegment(sketch, "E374.rect.left", {"start": v(45.56, -38.42) * mm, "end": v(45.56, -35.24) * mm});
            skLineSegment(sketch, "E375", {"start": v(-38.78, -35.24) * mm, "end": v(-38.78, -38.42) * mm});
            skArc(sketch, "E376.trimOffspring", {"start": v(46.78, -40.77) * mm, "mid": v(69.36, -45.17) * mm, "end": v(71.44, -22.25) * mm});
            skLineSegment(sketch, "E377", {"start": v(46.78, -40.77) * mm, "end": v(-48, -40.77) * mm});
            skLineSegment(sketch, "E378", {"start": v(-0.61, -40.77) * mm, "end": v(-0.61, -30.77) * mm, "construction": true});
            skLineSegment(sketch, "E379", {"start": v(-0.61, -30.77) * mm, "end": v(-0.61, -20.77) * mm, "construction": true});
            skLineSegment(sketch, "E380", {"start": v(-0.61, -20.77) * mm, "end": v(-0.61, -12.77) * mm, "construction": true});
            skLineSegment(sketch, "E381", {"start": v(-0.61, -12.77) * mm, "end": v(-0.61, 4.23) * mm, "construction": true});
            skLineSegment(sketch, "E382.rect.bottom", {"start": v(0.97, -30.77) * mm, "end": v(-2.2, -30.77) * mm});
            skLineSegment(sketch, "E382.rect.top", {"start": v(0.97, -20.77) * mm, "end": v(-2.2, -20.77) * mm});
            skLineSegment(sketch, "E382.rect.left", {"start": v(0.97, -30.77) * mm, "end": v(0.97, -20.77) * mm});
            skLineSegment(sketch, "E382.rect.right", {"start": v(-2.2, -30.77) * mm, "end": v(-2.2, -20.77) * mm});
            skPoint(sketch, "E382.rect.middle", {"position": v(-0.61, -25.77) * mm});
            skLineSegment(sketch, "E383.rect.bottom", {"start": v(0.97, -12.77) * mm, "end": v(-2.2, -12.77) * mm});
            skLineSegment(sketch, "E383.rect.top", {"start": v(0.97, 4.23) * mm, "end": v(-2.2, 4.23) * mm});
            skLineSegment(sketch, "E383.rect.left", {"start": v(0.97, -12.77) * mm, "end": v(0.97, 4.23) * mm});
            skLineSegment(sketch, "E383.rect.right", {"start": v(-2.2, -12.77) * mm, "end": v(-2.2, 4.23) * mm});
            skPoint(sketch, "E383.rect.middle", {"position": v(-0.61, -4.27) * mm});
            skLineSegment(sketch, "E384", {"start": v(37.56, -35.24) * mm, "end": v(37.56, -38.42) * mm});
            skSolve(sketch);
        }
        {
            var Q0;
            Q0=makeQuery(id+"F2.imprint","IMPRINT",FACE,{"disambiguationData":[TD([[makeQuery(id+"F2.imprint","IMPRINT",EDGE,{"derivedFrom":sQuery(id+"F2.wireOp",EDGE,"E207.0")}),1.0]])]});
            extrude(context, id + "F3", {"entities" : qUnion([Q0]), "oppositeDirection" : true, "depth" : 3.17 * mm});
        }
        {
            var Q0;
            Q0=qCreatedBy(makeId("Front.planeOp"),FACE);
            var sketch = newSketch(context, id + "F4", { "sketchPlane" : qUnion([Q0])});
            skLineSegment(sketch, "E385.bottom", {"start": v(-44.96, 53.62) * mm, "end": v(-43.96, 53.62) * mm});
            skLineSegment(sketch, "E385.top", {"start": v(-44.96, 16.62) * mm, "end": v(-43.96, 16.62) * mm});
            skLineSegment(sketch, "E385.left", {"start": v(-44.96, 53.62) * mm, "end": v(-44.96, 16.62) * mm});
            skLineSegment(sketch, "E385.right", {"start": v(-34.96, 53.62) * mm, "end": v(-34.96, 16.62) * mm});
            skLineSegment(sketch, "E386.rect.top", {"start": v(-36.02, 56.8) * mm, "end": v(-44.02, 56.8) * mm});
            skPoint(sketch, "E386.rect.middle", {"position": v(-39.96, 53.62) * mm});
            skLineSegment(sketch, "E387.rect.bottom", {"start": v(-36, 13.45) * mm, "end": v(-44, 13.45) * mm});
            skLineSegment(sketch, "E387.rect.left", {"start": v(-36, 13.45) * mm, "end": v(-35.96, 16.62) * mm});
            skLineSegment(sketch, "E387.rect.right", {"start": v(-44, 13.45) * mm, "end": v(-43.96, 16.62) * mm});
            skPoint(sketch, "E387.rect.middle", {"position": v(-39.96, 16.62) * mm});
            skLineSegment(sketch, "E388", {"start": v(-35.96, 53.62) * mm, "end": v(-36.02, 56.8) * mm});
            skLineSegment(sketch, "E389", {"start": v(-43.96, 53.62) * mm, "end": v(-44.02, 56.8) * mm});
            skLineSegment(sketch, "E390.trimOffspring", {"start": v(-35.96, 16.62) * mm, "end": v(-34.96, 16.62) * mm});
            skLineSegment(sketch, "E391.trimOffspring", {"start": v(-35.96, 53.62) * mm, "end": v(-34.96, 53.62) * mm});
            skLineSegment(sketch, "E392", {"start": v(-44.96, 35.12) * mm, "end": v(-34.96, 35.12) * mm, "construction": true});
            skSolve(sketch);
        }
        {
            var Q0;
            Q0=makeQuery(id+"F4.imprint","IMPRINT",FACE,{"disambiguationData":[TD([[makeQuery(id+"F4.imprint","IMPRINT",EDGE,{"derivedFrom":sQuery(id+"F4.wireOp",EDGE,"E385.bottom")}),-1.0]])]});
            extrude(context, id + "F5", {"entities" : qUnion([Q0]), "depth" : 3.17 * mm});
        }
        {
            var Q0;
            Q0=qCreatedBy(makeId("Right.planeOp"),FACE);
            var sketch = newSketch(context, id + "F6", { "sketchPlane" : qUnion([Q0])});
            skLineSegment(sketch, "E393.bottom", {"start": v(-40.79, 0) * mm, "end": v(19.21, 0) * mm});
            skLineSegment(sketch, "E393.top", {"start": v(-40.79, 55) * mm, "end": v(19.21, 55) * mm});
            skLineSegment(sketch, "E393.left", {"start": v(-40.79, 0) * mm, "end": v(-40.79, 55) * mm});
            skLineSegment(sketch, "E393.right", {"start": v(19.21, 0) * mm, "end": v(19.21, 55) * mm});
            skLineSegment(sketch, "E394.bottom", {"start": v(-40.79, 0) * mm, "end": v(-30.79, 0) * mm});
            skLineSegment(sketch, "E394.top", {"start": v(-40.79, 3.17) * mm, "end": v(-30.79, 3.17) * mm});
            skLineSegment(sketch, "E394.left", {"start": v(-40.79, 0) * mm, "end": v(-40.79, 3.17) * mm});
            skLineSegment(sketch, "E394.right", {"start": v(-30.79, 0) * mm, "end": v(-30.79, 3.17) * mm});
            skLineSegment(sketch, "E395.bottom", {"start": v(19.21, 2.95) * mm, "end": v(4.21, 2.95) * mm});
            skLineSegment(sketch, "E395.top", {"start": v(19.21, 0) * mm, "end": v(4.21, 0) * mm});
            skLineSegment(sketch, "E395.left", {"start": v(19.21, 2.95) * mm, "end": v(19.21, 0) * mm});
            skLineSegment(sketch, "E395.right", {"start": v(4.21, 2.95) * mm, "end": v(4.21, 0) * mm});
            skLineSegment(sketch, "E396.bottom", {"start": v(-20.79, 0) * mm, "end": v(-12.79, 0) * mm});
            skLineSegment(sketch, "E396.top", {"start": v(-20.79, 3.27) * mm, "end": v(-12.79, 3.27) * mm});
            skLineSegment(sketch, "E396.left", {"start": v(-20.79, 0) * mm, "end": v(-20.79, 3.27) * mm});
            skLineSegment(sketch, "E396.right", {"start": v(-12.79, 0) * mm, "end": v(-12.79, 3.27) * mm});
            skLineSegment(sketch, "E397", {"start": v(-30.79, 3.17) * mm, "end": v(-20.79, 3.27) * mm, "construction": true});
            skLineSegment(sketch, "E398", {"start": v(-12.79, 3.27) * mm, "end": v(4.21, 2.95) * mm, "construction": true});
            skLineSegment(sketch, "E399", {"start": v(11.71, 2.95) * mm, "end": v(11.71, 39.95) * mm, "construction": true});
            skLineSegment(sketch, "E400.bottom", {"start": v(19.21, 39.95) * mm, "end": v(7.13, 39.95) * mm});
            skLineSegment(sketch, "E400.top", {"start": v(19.21, 43.12) * mm, "end": v(7.13, 43.12) * mm});
            skLineSegment(sketch, "E400.left", {"start": v(19.21, 39.95) * mm, "end": v(19.21, 43.12) * mm});
            skLineSegment(sketch, "E400.right", {"start": v(7.13, 39.95) * mm, "end": v(7.13, 43.12) * mm});
            skLineSegment(sketch, "E401", {"start": v(7.13, 41.54) * mm, "end": v(-40.79, 41.54) * mm, "construction": true});
            skSolve(sketch);
        }
        {
            var Q0;
            Q0=makeQuery(id+"F6.imprint","IMPRINT",FACE,{"disambiguationData":[TD([[makeQuery(id+"F6.imprint","IMPRINT",EDGE,{"derivedFrom":sQuery(id+"F6.wireOp",EDGE,"E393.top")}),-1.0]])]});
            extrude(context, id + "F7", {"entities" : qUnion([Q0]), "depth" : 3.17 * mm});
        }
    });
